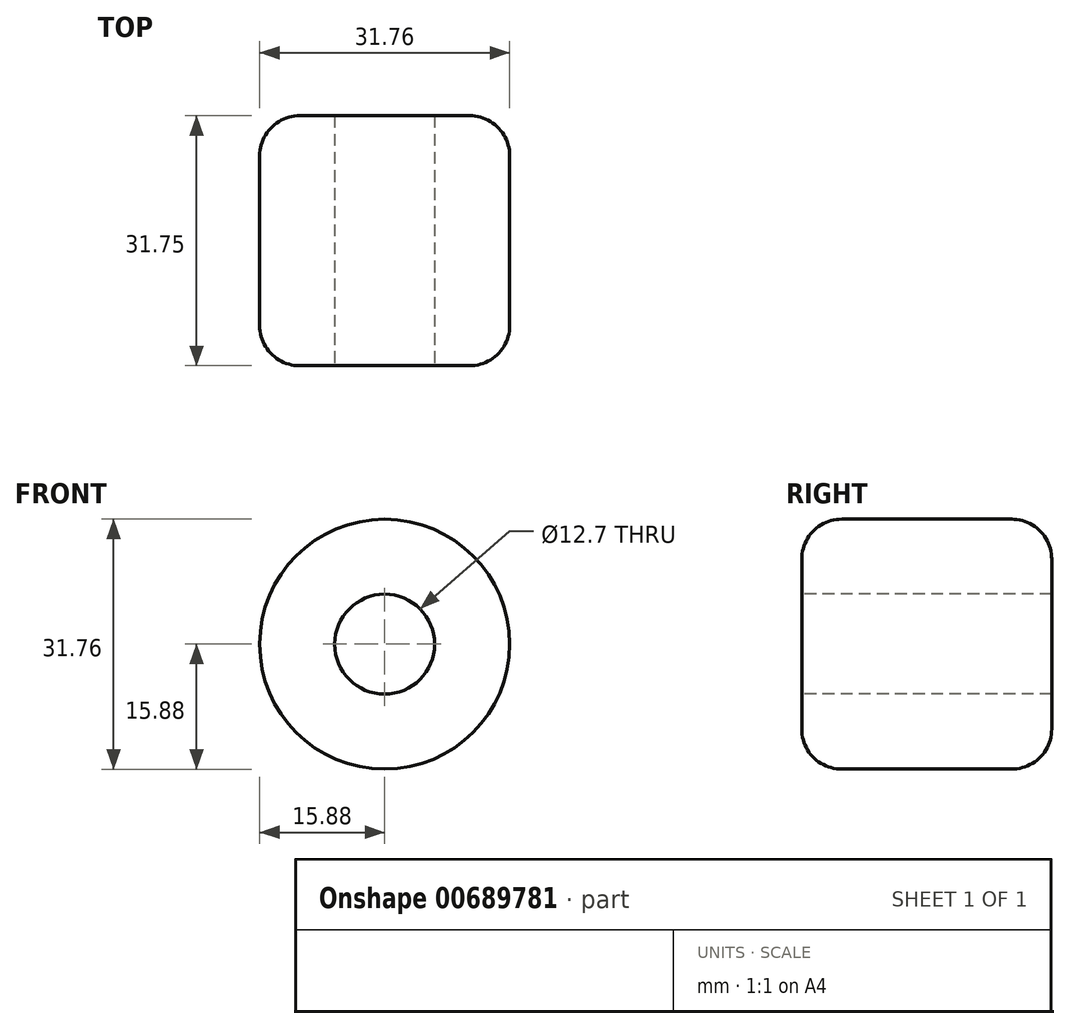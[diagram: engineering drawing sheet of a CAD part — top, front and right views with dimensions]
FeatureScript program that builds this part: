
annotation { "Feature Type Name" : "Feature", "Feature Type Description" : "" }
export const myFeature = defineFeature(function(context is Context, id is Id, definition is map)
    precondition{}
    {
        {
            var Q0;
            Q0=qCreatedBy(makeId("Front.planeOp"),FACE);
            var sketch = newSketch(context, id + "F0", { "sketchPlane" : qUnion([Q0])});
            skCircle(sketch, "E0", {"center": v(0, 0) * mm, "radius": 15.88 * mm});
            skSolve(sketch);
        }
        {
            var Q0;
            Q0 = qSketchRegion(id + "F0", true);
            var Q1;
            Q1=makeQuery(id+"F0.imprint","IMPRINT",FACE,{"disambiguationData":[TD([[makeQuery(id+"F0.imprint","IMPRINT",EDGE,{"derivedFrom":sQuery(id+"F0.wireOp",EDGE,"E0")}),1.0]])]});
            extrude(context, id + "F1", {"entities" : qUnion([Q0, Q1]), "depth" : 31.75 * mm, "offsetDistance" : 25.4 * mm});
        }
        {
            var Q0;
            Q0=qCreatedBy(makeId("Front.planeOp"),FACE);
            var sketch = newSketch(context, id + "F2", { "sketchPlane" : qUnion([Q0])});
            skCircle(sketch, "E1", {"center": v(0, 0) * mm, "radius": 4.26 * mm});
            skSolve(sketch);
        }
        {
            var Q0;
            Q0=sQuery(id+"F2.wireOp",VERTEX,"E1.center");
            var Q1;
            Q1=makeQuery(id+"F1.opExtrude","SWEPT_BODY",BODY,{"disambiguationData":[OSD([sQuery(id+"F0.wireOp",EDGE,"E0")])]});
            hole(context, id + "F3", {"style" : HoleStyle.SIMPLE, "endStyle" : HoleEndStyle.THROUGH, "oppositeDirection" : true, "holeDiameter" : 12.7 * mm, "majorDiameter" : 6.35 * mm, "isTappedThrough" : true, "tappedDepth" : 12.7 * mm, "tapClearance" : 3, "locations" : qUnion([Q0]), "scope" : qUnion([Q1]), "startStyle" : HoleStartStyle.PART});
        }
        {
            var Q0;
            Q0=makeQuery(id+"F1.opExtrude","CAP_EDGE",EDGE,{"disambiguationData":[OSD([sQuery(id+"F0.wireOp",EDGE,"E0")])],"isStart":false});
            var Q1;
            Q1=makeQuery(id+"F1.opExtrude","CAP_EDGE",EDGE,{"disambiguationData":[OSD([sQuery(id+"F0.wireOp",EDGE,"E0")])],"isStart":true});
            fillet(context, id + "F4", {"entities" : qUnion([Q0, Q1]), "radius" : 5.08 * mm, "tangentPropagation" : true, "allowEdgeOverflow" : false});
        }
    });
